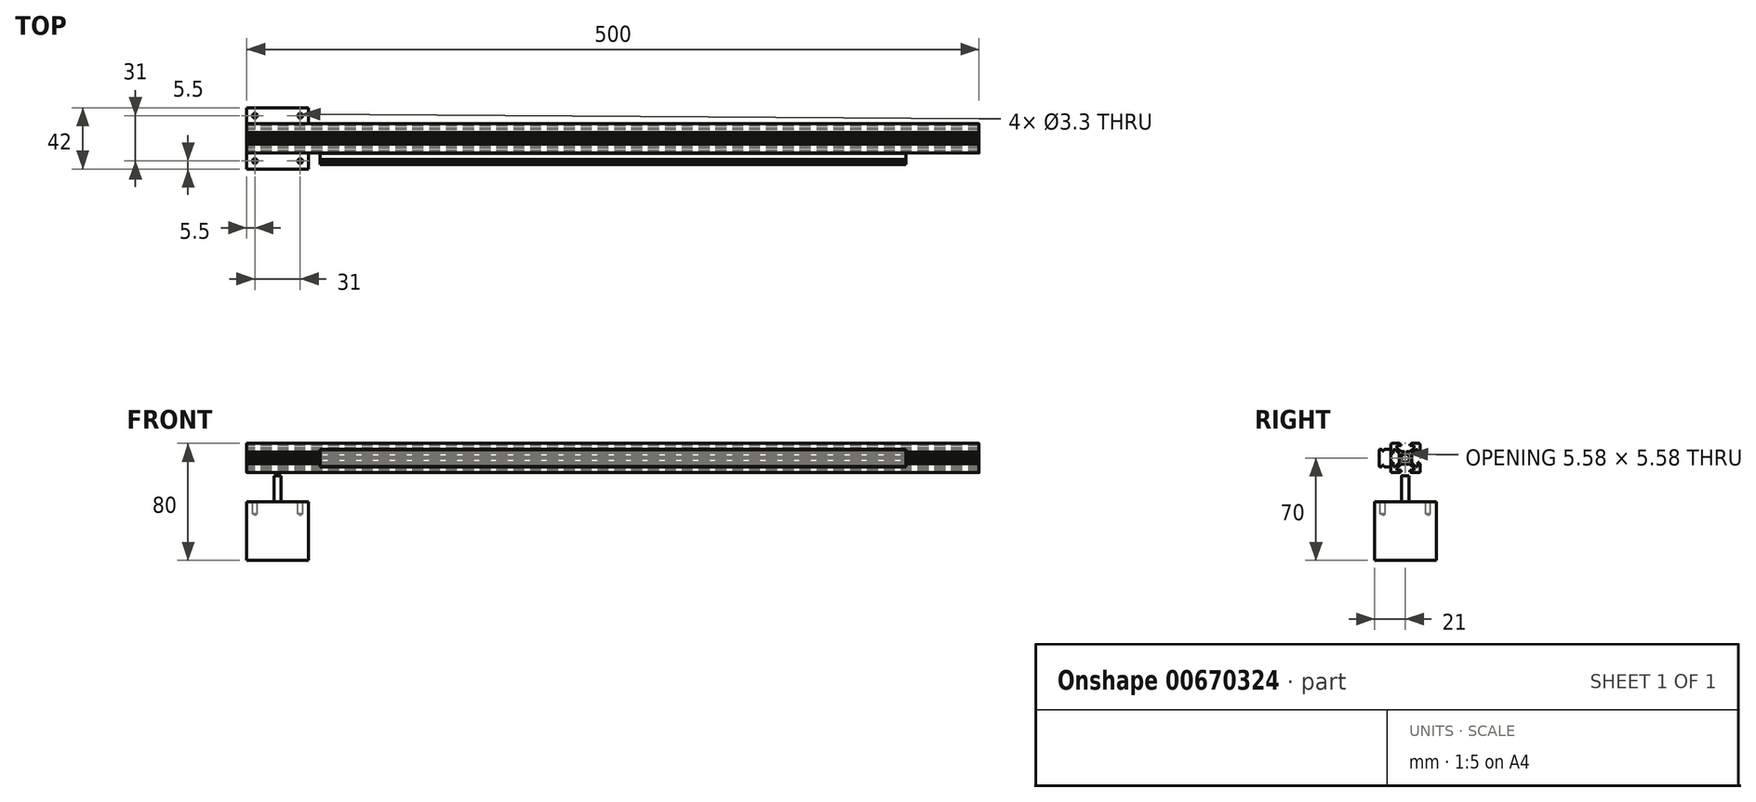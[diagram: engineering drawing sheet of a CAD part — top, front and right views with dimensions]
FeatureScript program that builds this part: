
annotation { "Feature Type Name" : "Feature", "Feature Type Description" : "" }
export const myFeature = defineFeature(function(context is Context, id is Id, definition is map)
    precondition{}
    {
        {
            var Q0;
            Q0=qCreatedBy(makeId("Right.planeOp"),FACE);
            var sketch = newSketch(context, id + "F0", { "sketchPlane" : qUnion([Q0])});
            skLineSegment(sketch, "E0.0", {"start": v(-4, 9.5) * mm, "end": v(-4, 10) * mm});
            skLineSegment(sketch, "E0.1", {"start": v(-3, 9.5) * mm, "end": v(-4, 9.5) * mm});
            skLineSegment(sketch, "E0.2", {"start": v(-3, 8.4) * mm, "end": v(-3, 9.5) * mm});
            skLineSegment(sketch, "E0.3", {"start": v(-5.8, 8.4) * mm, "end": v(-3, 8.4) * mm});
            skLineSegment(sketch, "E0.4", {"start": v(-5.8, 6.93) * mm, "end": v(-5.8, 8.4) * mm});
            skLineSegment(sketch, "E0.5", {"start": v(-3.12, 4.25) * mm, "end": v(-5.8, 6.93) * mm});
            skLineSegment(sketch, "E0.6", {"start": v(-0.75, 4.25) * mm, "end": v(-3.12, 4.25) * mm});
            skLineSegment(sketch, "E0.7", {"start": v(0, 3.85) * mm, "end": v(-0.75, 4.25) * mm});
            skLineSegment(sketch, "E0.8", {"start": v(0.75, 4.25) * mm, "end": v(0, 3.85) * mm});
            skLineSegment(sketch, "E0.9", {"start": v(3.12, 4.25) * mm, "end": v(0.75, 4.25) * mm});
            skLineSegment(sketch, "E0.10", {"start": v(5.8, 6.93) * mm, "end": v(3.12, 4.25) * mm});
            skLineSegment(sketch, "E0.11", {"start": v(5.8, 8.4) * mm, "end": v(5.8, 6.93) * mm});
            skLineSegment(sketch, "E0.12", {"start": v(3, 8.4) * mm, "end": v(5.8, 8.4) * mm});
            skLineSegment(sketch, "E0.13", {"start": v(3, 9.5) * mm, "end": v(3, 8.4) * mm});
            skLineSegment(sketch, "E0.14", {"start": v(4, 9.5) * mm, "end": v(3, 9.5) * mm});
            skLineSegment(sketch, "E0.15", {"start": v(4, 10) * mm, "end": v(4, 9.5) * mm});
            skLineSegment(sketch, "E0.16", {"start": v(9, 10) * mm, "end": v(4, 10) * mm});
            skArc(sketch, "E0.17", {"start": v(10, 9) * mm, "mid": v(9.7, 9.7) * mm, "end": v(9, 10) * mm});
            skLineSegment(sketch, "E0.18", {"start": v(10, 4) * mm, "end": v(10, 9) * mm});
            skLineSegment(sketch, "E0.19", {"start": v(9.5, 4) * mm, "end": v(10, 4) * mm});
            skLineSegment(sketch, "E0.20", {"start": v(9.5, 3) * mm, "end": v(9.5, 4) * mm});
            skLineSegment(sketch, "E0.21", {"start": v(8.4, 3) * mm, "end": v(9.5, 3) * mm});
            skLineSegment(sketch, "E0.22", {"start": v(8.4, 5.8) * mm, "end": v(8.4, 3) * mm});
            skLineSegment(sketch, "E0.23", {"start": v(6.93, 5.8) * mm, "end": v(8.4, 5.8) * mm});
            skLineSegment(sketch, "E0.24", {"start": v(4.25, 3.12) * mm, "end": v(6.93, 5.8) * mm});
            skLineSegment(sketch, "E0.25", {"start": v(4.25, 0.75) * mm, "end": v(4.25, 3.12) * mm});
            skLineSegment(sketch, "E0.26", {"start": v(3.85, 0) * mm, "end": v(4.25, 0.75) * mm});
            skLineSegment(sketch, "E0.27", {"start": v(4.25, -0.75) * mm, "end": v(3.85, 0) * mm});
            skLineSegment(sketch, "E0.28", {"start": v(4.25, -3.12) * mm, "end": v(4.25, -0.75) * mm});
            skLineSegment(sketch, "E0.29", {"start": v(-4, -10) * mm, "end": v(-4, -9.5) * mm});
            skLineSegment(sketch, "E0.30", {"start": v(-9, -10) * mm, "end": v(-4, -10) * mm});
            skArc(sketch, "E0.31", {"start": v(-10, -9) * mm, "mid": v(-9.7, -9.7) * mm, "end": v(-9, -10) * mm});
            skLineSegment(sketch, "E0.32", {"start": v(-10, -4) * mm, "end": v(-10, -9) * mm});
            skLineSegment(sketch, "E0.33", {"start": v(-9.5, -4) * mm, "end": v(-10, -4) * mm});
            skLineSegment(sketch, "E0.34", {"start": v(-9.5, -3) * mm, "end": v(-9.5, -4) * mm});
            skLineSegment(sketch, "E0.35", {"start": v(-8.4, -3) * mm, "end": v(-9.5, -3) * mm});
            skLineSegment(sketch, "E0.36", {"start": v(-8.4, -5.8) * mm, "end": v(-8.4, -3) * mm});
            skLineSegment(sketch, "E0.37", {"start": v(-6.93, -5.8) * mm, "end": v(-8.4, -5.8) * mm});
            skLineSegment(sketch, "E0.38", {"start": v(-4.25, -3.12) * mm, "end": v(-6.93, -5.8) * mm});
            skLineSegment(sketch, "E0.39", {"start": v(-4.25, -0.75) * mm, "end": v(-4.25, -3.12) * mm});
            skLineSegment(sketch, "E0.40", {"start": v(-3.85, 0) * mm, "end": v(-4.25, -0.75) * mm});
            skLineSegment(sketch, "E0.41", {"start": v(-9.5, 4) * mm, "end": v(-9.5, 3) * mm});
            skLineSegment(sketch, "E0.42", {"start": v(-4, 10) * mm, "end": v(-9, 10) * mm});
            skLineSegment(sketch, "E0.43", {"start": v(-10, 4) * mm, "end": v(-9.5, 4) * mm});
            skLineSegment(sketch, "E0.44", {"start": v(-10, 9) * mm, "end": v(-10, 4) * mm});
            skArc(sketch, "E0.45", {"start": v(-9, 10) * mm, "mid": v(-9.7, 9.7) * mm, "end": v(-10, 9) * mm});
            skLineSegment(sketch, "E0.46", {"start": v(-9.5, 3) * mm, "end": v(-8.4, 3) * mm});
            skLineSegment(sketch, "E0.47", {"start": v(-8.4, 3) * mm, "end": v(-8.4, 5.8) * mm});
            skLineSegment(sketch, "E0.48", {"start": v(-8.4, 5.8) * mm, "end": v(-6.93, 5.8) * mm});
            skLineSegment(sketch, "E0.49", {"start": v(-6.93, 5.8) * mm, "end": v(-4.25, 3.12) * mm});
            skLineSegment(sketch, "E0.50", {"start": v(-4.25, 3.12) * mm, "end": v(-4.25, 0.75) * mm});
            skLineSegment(sketch, "E0.51", {"start": v(-4.25, 0.75) * mm, "end": v(-3.85, 0) * mm});
            skLineSegment(sketch, "E0.52", {"start": v(-4, -9.5) * mm, "end": v(-3, -9.5) * mm});
            skLineSegment(sketch, "E0.53", {"start": v(-3, -9.5) * mm, "end": v(-3, -8.4) * mm});
            skLineSegment(sketch, "E0.54", {"start": v(-3, -8.4) * mm, "end": v(-5.8, -8.4) * mm});
            skLineSegment(sketch, "E0.55", {"start": v(-5.8, -8.4) * mm, "end": v(-5.8, -6.93) * mm});
            skLineSegment(sketch, "E0.56", {"start": v(-5.8, -6.93) * mm, "end": v(-3.12, -4.25) * mm});
            skLineSegment(sketch, "E0.57", {"start": v(-3.12, -4.25) * mm, "end": v(-0.75, -4.25) * mm});
            skLineSegment(sketch, "E0.58", {"start": v(-0.75, -4.25) * mm, "end": v(0, -3.85) * mm});
            skLineSegment(sketch, "E0.59", {"start": v(0, -3.85) * mm, "end": v(0.75, -4.25) * mm});
            skLineSegment(sketch, "E0.60", {"start": v(0.75, -4.25) * mm, "end": v(3.12, -4.25) * mm});
            skLineSegment(sketch, "E0.61", {"start": v(3.12, -4.25) * mm, "end": v(5.8, -6.93) * mm});
            skLineSegment(sketch, "E0.62", {"start": v(5.8, -6.93) * mm, "end": v(5.8, -8.4) * mm});
            skLineSegment(sketch, "E0.63", {"start": v(5.8, -8.4) * mm, "end": v(3, -8.4) * mm});
            skLineSegment(sketch, "E0.64", {"start": v(3, -8.4) * mm, "end": v(3, -9.5) * mm});
            skLineSegment(sketch, "E0.65", {"start": v(3, -9.5) * mm, "end": v(4, -9.5) * mm});
            skLineSegment(sketch, "E0.66", {"start": v(4, -9.5) * mm, "end": v(4, -10) * mm});
            skLineSegment(sketch, "E0.67", {"start": v(4, -10) * mm, "end": v(9, -10) * mm});
            skArc(sketch, "E0.68", {"start": v(9, -10) * mm, "mid": v(9.7, -9.7) * mm, "end": v(10, -9) * mm});
            skLineSegment(sketch, "E0.69", {"start": v(10, -9) * mm, "end": v(10, -4) * mm});
            skLineSegment(sketch, "E0.70", {"start": v(10, -4) * mm, "end": v(9.5, -4) * mm});
            skLineSegment(sketch, "E0.71", {"start": v(9.5, -4) * mm, "end": v(9.5, -3) * mm});
            skLineSegment(sketch, "E0.72", {"start": v(9.5, -3) * mm, "end": v(8.4, -3) * mm});
            skLineSegment(sketch, "E0.73", {"start": v(8.4, -3) * mm, "end": v(8.4, -5.8) * mm});
            skLineSegment(sketch, "E0.74", {"start": v(8.4, -5.8) * mm, "end": v(6.93, -5.8) * mm});
            skLineSegment(sketch, "E0.75", {"start": v(6.93, -5.8) * mm, "end": v(4.25, -3.12) * mm});
            skLineSegment(sketch, "E1.0", {"start": v(1.66, 2.79) * mm, "end": v(1.3, 2.43) * mm});
            skArc(sketch, "E1.1", {"start": v(2.79, 1.66) * mm, "mid": v(2.3, 2.3) * mm, "end": v(1.66, 2.79) * mm});
            skLineSegment(sketch, "E1.2", {"start": v(2.79, 1.66) * mm, "end": v(2.43, 1.3) * mm});
            skArc(sketch, "E1.3", {"start": v(2.43, -1.3) * mm, "mid": v(2.75, 0) * mm, "end": v(2.43, 1.3) * mm});
            skLineSegment(sketch, "E1.4", {"start": v(2.79, -1.66) * mm, "end": v(2.43, -1.3) * mm});
            skArc(sketch, "E1.5", {"start": v(-2.43, 1.3) * mm, "mid": v(-2.75, 0) * mm, "end": v(-2.43, -1.3) * mm});
            skLineSegment(sketch, "E1.6", {"start": v(-2.79, 1.66) * mm, "end": v(-2.43, 1.3) * mm});
            skArc(sketch, "E1.7", {"start": v(-1.66, 2.79) * mm, "mid": v(-2.3, 2.3) * mm, "end": v(-2.79, 1.66) * mm});
            skLineSegment(sketch, "E1.8", {"start": v(-1.66, 2.79) * mm, "end": v(-1.3, 2.43) * mm});
            skLineSegment(sketch, "E1.9", {"start": v(-2.79, -1.66) * mm, "end": v(-2.43, -1.3) * mm});
            skArc(sketch, "E1.10", {"start": v(-2.79, -1.66) * mm, "mid": v(-2.3, -2.3) * mm, "end": v(-1.66, -2.79) * mm});
            skLineSegment(sketch, "E1.11", {"start": v(-1.66, -2.79) * mm, "end": v(-1.3, -2.43) * mm});
            skArc(sketch, "E1.12", {"start": v(-1.3, -2.43) * mm, "mid": v(0, -2.75) * mm, "end": v(1.3, -2.43) * mm});
            skLineSegment(sketch, "E1.13", {"start": v(1.66, -2.79) * mm, "end": v(1.3, -2.43) * mm});
            skArc(sketch, "E1.14", {"start": v(1.3, 2.43) * mm, "mid": v(0, 2.75) * mm, "end": v(-1.3, 2.43) * mm});
            skArc(sketch, "E1.15", {"start": v(1.66, -2.79) * mm, "mid": v(2.3, -2.3) * mm, "end": v(2.79, -1.66) * mm});
            skSolve(sketch);
        }
        {
            var Q0;
            Q0=makeQuery(id+"F0.imprint","IMPRINT",FACE,{"disambiguationData":[TD([[makeQuery(id+"F0.imprint","IMPRINT",EDGE,{"derivedFrom":sQuery(id+"F0.wireOp",EDGE,"E0.0")}),1.0]])]});
            extrude(context, id + "F1", {"entities" : qUnion([Q0]), "depth" : 250 * mm, "offsetDistance" : 25 * mm, "hasSecondDirection" : true, "secondDirectionOppositeDirection" : true, "secondDirectionDepth" : 250 * mm});
        }
        {
            var Q0;
            Q0=qCreatedBy(makeId("Right.planeOp"),FACE);
            var sketch = newSketch(context, id + "F2", { "sketchPlane" : qUnion([Q0])});
            skLineSegment(sketch, "E2.0", {"start": v(-5.7, 3.16) * mm, "end": v(-6, 2.86) * mm});
            skLineSegment(sketch, "E2.1", {"start": v(5.7, 3.16) * mm, "end": v(-5.7, 3.16) * mm});
            skLineSegment(sketch, "E2.2", {"start": v(6, 2.86) * mm, "end": v(5.7, 3.16) * mm});
            skLineSegment(sketch, "E2.3", {"start": v(6, 1.61) * mm, "end": v(6, 2.86) * mm});
            skArc(sketch, "E2.4", {"start": v(5.3, 0.88) * mm, "mid": v(5.56, 1.33) * mm, "end": v(6, 1.61) * mm});
            skLineSegment(sketch, "E2.5", {"start": v(-6, 2.86) * mm, "end": v(-6, 1.61) * mm});
            skLineSegment(sketch, "E2.6", {"start": v(4.69, 0.88) * mm, "end": v(5.3, 0.88) * mm});
            skLineSegment(sketch, "E2.7", {"start": v(4.69, 0.24) * mm, "end": v(4.69, 0.88) * mm});
            skLineSegment(sketch, "E2.8", {"start": v(5.3, 0.24) * mm, "end": v(4.69, 0.24) * mm});
            skArc(sketch, "E2.9", {"start": v(6, -0.5) * mm, "mid": v(5.55, -0.22) * mm, "end": v(5.3, 0.24) * mm});
            skLineSegment(sketch, "E2.10", {"start": v(-4.69, 0.24) * mm, "end": v(-5.3, 0.24) * mm});
            skLineSegment(sketch, "E2.11", {"start": v(-4.69, 0.88) * mm, "end": v(-4.69, 0.24) * mm});
            skLineSegment(sketch, "E2.12", {"start": v(-5.3, 0.88) * mm, "end": v(-4.69, 0.88) * mm});
            skArc(sketch, "E2.13", {"start": v(-6, 1.61) * mm, "mid": v(-5.56, 1.33) * mm, "end": v(-5.3, 0.88) * mm});
            skArc(sketch, "E2.14", {"start": v(-5.3, 0.24) * mm, "mid": v(-5.55, -0.22) * mm, "end": v(-6, -0.5) * mm});
            skLineSegment(sketch, "E2.15", {"start": v(-6, -0.5) * mm, "end": v(-6, -4.54) * mm});
            skLineSegment(sketch, "E2.16", {"start": v(-6, -4.54) * mm, "end": v(-5.7, -4.84) * mm});
            skLineSegment(sketch, "E2.17", {"start": v(-5.7, -4.84) * mm, "end": v(5.7, -4.84) * mm});
            skLineSegment(sketch, "E2.18", {"start": v(5.7, -4.84) * mm, "end": v(6, -4.54) * mm});
            skLineSegment(sketch, "E2.19", {"start": v(6, -4.54) * mm, "end": v(6, -0.5) * mm});
            skSolve(sketch);
        }
        {
            var Q0;
            Q0=makeQuery(id+"F2.imprint","IMPRINT",FACE,{"disambiguationData":[TD([[makeQuery(id+"F2.imprint","IMPRINT",EDGE,{"derivedFrom":sQuery(id+"F2.wireOp",EDGE,"E2.0")}),1.0]])]});
            extrude(context, id + "F3", {"entities" : qUnion([Q0]), "depth" : 10 * mm, "offsetDistance" : 25 * mm, "hasSecondDirection" : true, "secondDirectionOppositeDirection" : true, "secondDirectionDepth" : 10 * mm});
        }
        {
            var Q0;
            Q0=qCreatedBy(makeId("Top.planeOp"),FACE);
            var sketch = newSketch(context, id + "F4", { "sketchPlane" : qUnion([Q0])});
            skLineSegment(sketch, "E3", {"start": v(-83.37, 0) * mm, "end": v(116.85, 0) * mm});
            skSolve(sketch);
        }
        {
            var Q0;
            Q0=makeQuery(id+"F3.opExtrude","SWEPT_BODY",BODY,{"disambiguationData":[OSD([sQuery(id+"F2.wireOp",EDGE,"E2.0"),sQuery(id+"F2.wireOp",EDGE,"E2.1"),sQuery(id+"F2.wireOp",EDGE,"E2.2"),sQuery(id+"F2.wireOp",EDGE,"E2.3"),sQuery(id+"F2.wireOp",EDGE,"E2.4"),sQuery(id+"F2.wireOp",EDGE,"E2.5"),sQuery(id+"F2.wireOp",EDGE,"E2.6"),sQuery(id+"F2.wireOp",EDGE,"E2.7"),sQuery(id+"F2.wireOp",EDGE,"E2.8"),sQuery(id+"F2.wireOp",EDGE,"E2.9"),sQuery(id+"F2.wireOp",EDGE,"E2.10"),sQuery(id+"F2.wireOp",EDGE,"E2.11"),sQuery(id+"F2.wireOp",EDGE,"E2.12"),sQuery(id+"F2.wireOp",EDGE,"E2.13"),sQuery(id+"F2.wireOp",EDGE,"E2.14"),sQuery(id+"F2.wireOp",EDGE,"E2.15"),sQuery(id+"F2.wireOp",EDGE,"E2.16"),sQuery(id+"F2.wireOp",EDGE,"E2.17"),sQuery(id+"F2.wireOp",EDGE,"E2.18"),sQuery(id+"F2.wireOp",EDGE,"E2.19")])]});
            var Q1;
            Q1=sQuery(id+"F4.wireOp",EDGE,"E3");
            transform(context, id + "F5", {"entities" : qUnion([Q0]), "transformType" : TransformType.ROTATION, "transformAxis" : qUnion([Q1]), "angle" : 90 * degree, "makeCopy" : false});
        }
        {
            var Q0;
            Q0=makeQuery(id+"F3.opExtrude","SWEPT_BODY",BODY,{"disambiguationData":[OSD([sQuery(id+"F2.wireOp",EDGE,"E2.0"),sQuery(id+"F2.wireOp",EDGE,"E2.1"),sQuery(id+"F2.wireOp",EDGE,"E2.2"),sQuery(id+"F2.wireOp",EDGE,"E2.3"),sQuery(id+"F2.wireOp",EDGE,"E2.4"),sQuery(id+"F2.wireOp",EDGE,"E2.5"),sQuery(id+"F2.wireOp",EDGE,"E2.6"),sQuery(id+"F2.wireOp",EDGE,"E2.7"),sQuery(id+"F2.wireOp",EDGE,"E2.8"),sQuery(id+"F2.wireOp",EDGE,"E2.9"),sQuery(id+"F2.wireOp",EDGE,"E2.10"),sQuery(id+"F2.wireOp",EDGE,"E2.11"),sQuery(id+"F2.wireOp",EDGE,"E2.12"),sQuery(id+"F2.wireOp",EDGE,"E2.13"),sQuery(id+"F2.wireOp",EDGE,"E2.14"),sQuery(id+"F2.wireOp",EDGE,"E2.15"),sQuery(id+"F2.wireOp",EDGE,"E2.16"),sQuery(id+"F2.wireOp",EDGE,"E2.17"),sQuery(id+"F2.wireOp",EDGE,"E2.18"),sQuery(id+"F2.wireOp",EDGE,"E2.19")])]});
            transform(context, id + "F6", {"entities" : qUnion([Q0]), "transformType" : TransformType.TRANSLATION_3D, "dx" : 0 * mm, "dy" : -14.84 * mm, "dz" : 0 * mm, "makeCopy" : false});
        }
        {
            var Q0;
            Q0=makeQuery(id+"F3.opExtrude","CAP_FACE",FACE,{"disambiguationData":[OSD([sQuery(id+"F2.wireOp",EDGE,"E2.0"),sQuery(id+"F2.wireOp",EDGE,"E2.1"),sQuery(id+"F2.wireOp",EDGE,"E2.2"),sQuery(id+"F2.wireOp",EDGE,"E2.3"),sQuery(id+"F2.wireOp",EDGE,"E2.4"),sQuery(id+"F2.wireOp",EDGE,"E2.5"),sQuery(id+"F2.wireOp",EDGE,"E2.6"),sQuery(id+"F2.wireOp",EDGE,"E2.7"),sQuery(id+"F2.wireOp",EDGE,"E2.8"),sQuery(id+"F2.wireOp",EDGE,"E2.9"),sQuery(id+"F2.wireOp",EDGE,"E2.10"),sQuery(id+"F2.wireOp",EDGE,"E2.11"),sQuery(id+"F2.wireOp",EDGE,"E2.12"),sQuery(id+"F2.wireOp",EDGE,"E2.13"),sQuery(id+"F2.wireOp",EDGE,"E2.14"),sQuery(id+"F2.wireOp",EDGE,"E2.15"),sQuery(id+"F2.wireOp",EDGE,"E2.16"),sQuery(id+"F2.wireOp",EDGE,"E2.17"),sQuery(id+"F2.wireOp",EDGE,"E2.18"),sQuery(id+"F2.wireOp",EDGE,"E2.19")])],"isStart":true});
            extrude(context, id + "F7", {"entities" : qUnion([Q0]), "operationType" : NewBodyOperationType.ADD, "depth" : 190 * mm, "offsetDistance" : 25 * mm});
        }
        {
            var Q0;
            Q0=makeQuery(id+"F3.opExtrude","CAP_FACE",FACE,{"disambiguationData":[OSD([sQuery(id+"F2.wireOp",EDGE,"E2.0"),sQuery(id+"F2.wireOp",EDGE,"E2.1"),sQuery(id+"F2.wireOp",EDGE,"E2.2"),sQuery(id+"F2.wireOp",EDGE,"E2.3"),sQuery(id+"F2.wireOp",EDGE,"E2.4"),sQuery(id+"F2.wireOp",EDGE,"E2.5"),sQuery(id+"F2.wireOp",EDGE,"E2.6"),sQuery(id+"F2.wireOp",EDGE,"E2.7"),sQuery(id+"F2.wireOp",EDGE,"E2.8"),sQuery(id+"F2.wireOp",EDGE,"E2.9"),sQuery(id+"F2.wireOp",EDGE,"E2.10"),sQuery(id+"F2.wireOp",EDGE,"E2.11"),sQuery(id+"F2.wireOp",EDGE,"E2.12"),sQuery(id+"F2.wireOp",EDGE,"E2.13"),sQuery(id+"F2.wireOp",EDGE,"E2.14"),sQuery(id+"F2.wireOp",EDGE,"E2.15"),sQuery(id+"F2.wireOp",EDGE,"E2.16"),sQuery(id+"F2.wireOp",EDGE,"E2.17"),sQuery(id+"F2.wireOp",EDGE,"E2.18"),sQuery(id+"F2.wireOp",EDGE,"E2.19")])],"isStart":false});
            extrude(context, id + "F8", {"entities" : qUnion([Q0]), "operationType" : NewBodyOperationType.ADD, "depth" : 190 * mm, "offsetDistance" : 25 * mm});
        }
        {
            var Q0;
            Q0=qCreatedBy(makeId("Front.planeOp"),FACE);
            var sketch = newSketch(context, id + "F9", { "sketchPlane" : qUnion([Q0])});
            skLineSegment(sketch, "E4.bottom", {"start": v(-250, -30) * mm, "end": v(-208, -30) * mm});
            skLineSegment(sketch, "E4.top", {"start": v(-250, -70) * mm, "end": v(-208, -70) * mm});
            skLineSegment(sketch, "E4.left", {"start": v(-250, -30) * mm, "end": v(-250, -70) * mm});
            skLineSegment(sketch, "E4.right", {"start": v(-208, -30) * mm, "end": v(-208, -70) * mm});
            skSolve(sketch);
        }
        {
            var Q0;
            Q0=makeQuery(id+"F9.imprint","IMPRINT",FACE,{"disambiguationData":[TD([[makeQuery(id+"F9.imprint","IMPRINT",EDGE,{"derivedFrom":sQuery(id+"F9.wireOp",EDGE,"E4.bottom")}),-1.0]])]});
            extrude(context, id + "F10", {"entities" : qUnion([Q0]), "depth" : 21 * mm, "offsetDistance" : 25 * mm, "hasSecondDirection" : true, "secondDirectionOppositeDirection" : true, "secondDirectionDepth" : 21 * mm});
        }
        {
            var Q0;
            Q0=makeQuery(id+"F10.opExtrude","SWEPT_FACE",FACE,{"disambiguationData":[OSD([sQuery(id+"F9.wireOp",EDGE,"E4.bottom")])]});
            var sketch = newSketch(context, id + "F11", { "sketchPlane" : qUnion([Q0])});
            skCircle(sketch, "E5", {"center": v(-229, 0) * mm, "radius": 2.5 * mm});
            skPoint(sketch, "E5.centerSnap0", {"position": v(-229, 21) * mm});
            skPoint(sketch, "E5.centerSnap1", {"position": v(-250, 0) * mm});
            skPoint(sketch, "E6", {"position": v(-244.5, 15.5) * mm});
            skPoint(sketch, "E7", {"position": v(-213.5, 15.5) * mm});
            skPoint(sketch, "E8", {"position": v(-213.5, -15.5) * mm});
            skPoint(sketch, "E9", {"position": v(-244.5, -15.5) * mm});
            skLineSegment(sketch, "E10", {"start": v(-229, 21) * mm, "end": v(-229, -21) * mm, "construction": true});
            skLineSegment(sketch, "E11", {"start": v(-229, -21) * mm, "end": v(-250, 0) * mm, "construction": true});
            skLineSegment(sketch, "E12", {"start": v(-208, 0) * mm, "end": v(-250, 0) * mm, "construction": true});
            skSolve(sketch);
        }
        {
            var Q0;
            Q0=makeQuery(id+"F11.imprint","IMPRINT",FACE,{"disambiguationData":[TD([[makeQuery(id+"F11.imprint","IMPRINT",EDGE,{"derivedFrom":sQuery(id+"F11.wireOp",EDGE,"E5")}),1.0]])]});
            extrude(context, id + "F12", {"entities" : qUnion([Q0]), "operationType" : NewBodyOperationType.ADD, "depth" : 18 * mm, "offsetDistance" : 25 * mm});
        }
        {
            var Q0;
            Q0=sQuery(id+"F11.wireOp",VERTEX,"E6");
            var Q1;
            Q1=sQuery(id+"F11.wireOp",VERTEX,"E9");
            var Q2;
            Q2=sQuery(id+"F11.wireOp",VERTEX,"E8");
            var Q3;
            Q3=sQuery(id+"F11.wireOp",VERTEX,"E7");
            var Q4;
            Q4=makeQuery(id+"F10.opExtrude","SWEPT_BODY",BODY,{"disambiguationData":[OSD([sQuery(id+"F9.wireOp",EDGE,"E4.bottom"),sQuery(id+"F9.wireOp",EDGE,"E4.top"),sQuery(id+"F9.wireOp",EDGE,"E4.left"),sQuery(id+"F9.wireOp",EDGE,"E4.right")])]});
            hole(context, id + "F13", {"style" : HoleStyle.SIMPLE, "endStyle" : HoleEndStyle.BLIND, "standardTappedOrClearance" : lookupTablePath({ "standard" : "ISO", "fit" : "Normal", "size" : "M3", "type" : "Clearance" }), "standardBlindInLast" : lookupTablePath({ "fit" : "Standard", "standard" : "ISO", "size" : "M3", "type" : "Clearance" }), "holeDiameter" : 3.3 * mm, "majorDiameter" : 5 * mm, "holeDepth" : 8 * mm, "isTappedThrough" : true, "tappedDepth" : 15 * mm, "tapClearance" : 0, "startFromSketch" : true, "locations" : qUnion([Q0, Q1, Q2, Q3]), "scope" : qUnion([Q4])});
        }
    });
